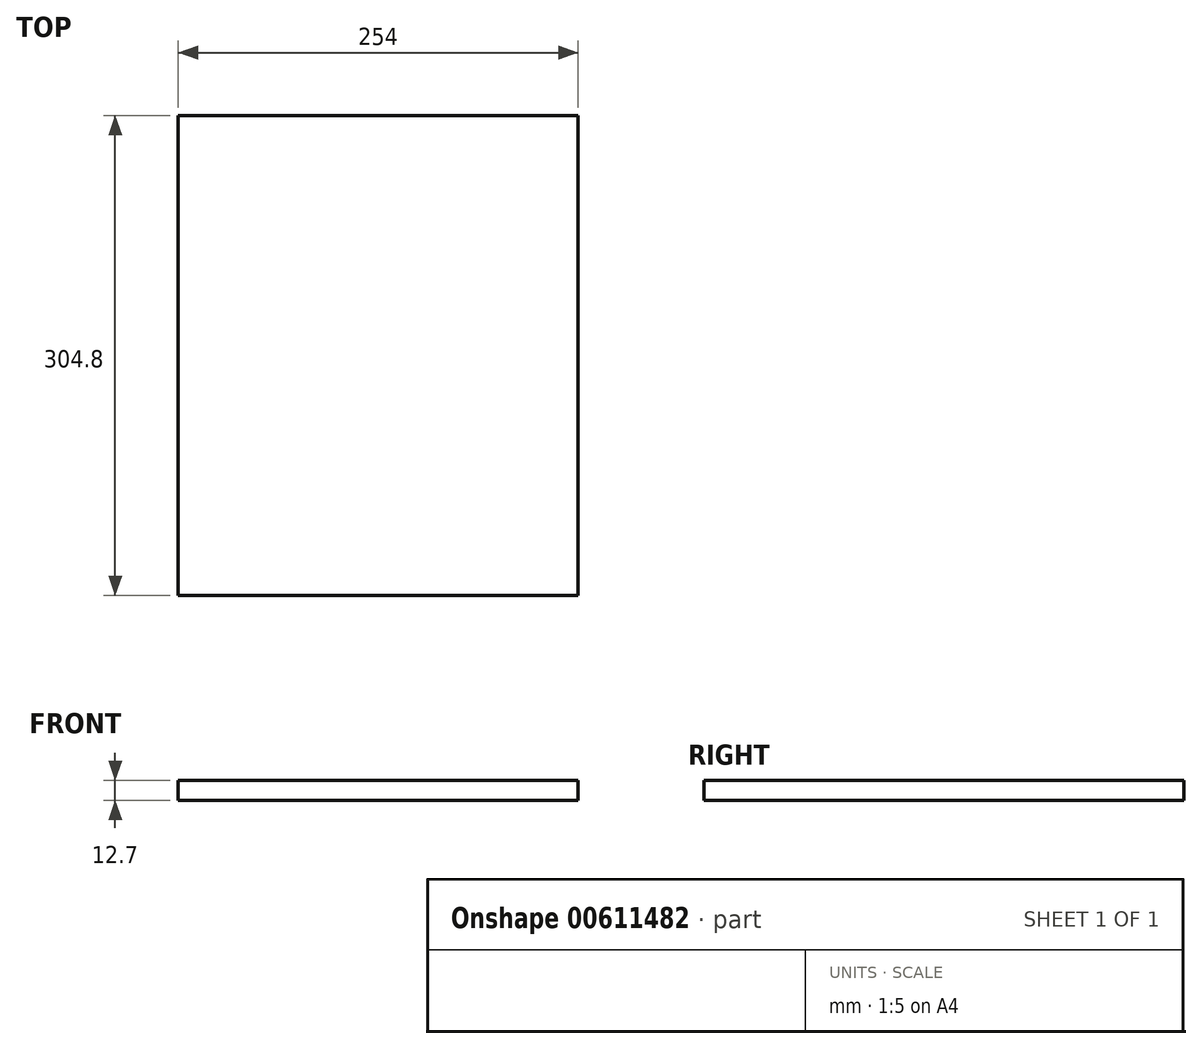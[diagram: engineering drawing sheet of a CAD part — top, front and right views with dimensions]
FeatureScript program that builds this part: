
annotation { "Feature Type Name" : "Feature", "Feature Type Description" : "" }
export const myFeature = defineFeature(function(context is Context, id is Id, definition is map)
    precondition{}
    {
        {
            var Q0;
            Q0=qCreatedBy(makeId("Front.planeOp"),FACE);
            var sketch = newSketch(context, id + "F0", { "sketchPlane" : qUnion([Q0])});
            skLineSegment(sketch, "E0.bottom", {"start": v(0, 0) * mm, "end": v(203.2, 0) * mm});
            skLineSegment(sketch, "E0.top", {"start": v(0, -12.7) * mm, "end": v(203.2, -12.7) * mm});
            skLineSegment(sketch, "E0.left", {"start": v(0, 0) * mm, "end": v(0, -12.7) * mm});
            skLineSegment(sketch, "E0.right", {"start": v(203.2, 0) * mm, "end": v(203.2, -12.7) * mm});
            skSolve(sketch);
        }
        {
            var Q0;
            Q0 = qSketchRegion(id + "F0", true);
            extrude(context, id + "F1", {"entities" : qUnion([Q0]), "depth" : 304.8 * mm, "offsetDistance" : 25.4 * mm});
        }
        {
            var Q0;
            Q0=makeQuery(id+"F1.opExtrude","SWEPT_FACE",FACE,{"disambiguationData":[OSD([sQuery(id+"F0.wireOp",EDGE,"E0.right")])]});
            extrude(context, id + "F2", {"entities" : qUnion([Q0]), "operationType" : NewBodyOperationType.ADD, "depth" : 50.8 * mm, "offsetDistance" : 25.4 * mm});
        }
    });
